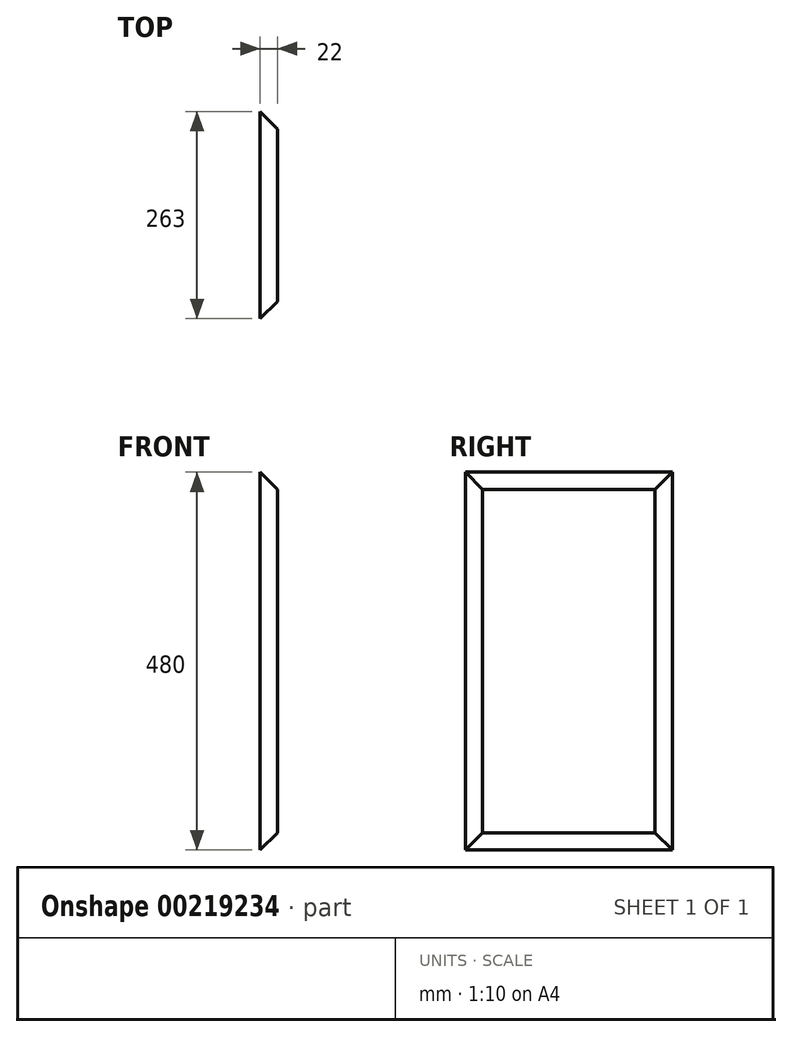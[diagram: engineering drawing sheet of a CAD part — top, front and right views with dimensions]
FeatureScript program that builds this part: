
annotation { "Feature Type Name" : "Feature", "Feature Type Description" : "" }
export const myFeature = defineFeature(function(context is Context, id is Id, definition is map)
    precondition{}
    {
        {
            var Q0;
            Q0=qCreatedBy(makeId("Right.planeOp"),FACE);
            var sketch = newSketch(context, id + "F0", { "sketchPlane" : qUnion([Q0])});
            skLineSegment(sketch, "E0.bottom", {"start": v(-131.5, 240) * mm, "end": v(131.5, 240) * mm});
            skLineSegment(sketch, "E0.top", {"start": v(-131.5, -240) * mm, "end": v(131.5, -240) * mm});
            skLineSegment(sketch, "E0.left", {"start": v(-131.5, 240) * mm, "end": v(-131.5, -240) * mm});
            skLineSegment(sketch, "E0.right", {"start": v(131.5, 240) * mm, "end": v(131.5, -240) * mm});
            skPoint(sketch, "E0.middle", {"position": v(0, 0) * mm});
            skSolve(sketch);
        }
        {
            var Q0;
            Q0=makeQuery(id+"F0.imprint","IMPRINT",FACE,{"disambiguationData":[TD([[makeQuery(id+"F0.imprint","IMPRINT",EDGE,{"derivedFrom":sQuery(id+"F0.wireOp",EDGE,"E0.bottom")}),-1.0]])]});
            extrude(context, id + "F1", {"entities" : qUnion([Q0]), "depth" : 22 * mm});
        }
        {
            var Q0;
            Q0=makeQuery(id+"F1.opExtrude","CAP_EDGE",EDGE,{"disambiguationData":[OSD([sQuery(id+"F0.wireOp",EDGE,"E0.left")])],"isStart":false});
            var Q1;
            Q1=makeQuery(id+"F1.opExtrude","CAP_EDGE",EDGE,{"disambiguationData":[OSD([sQuery(id+"F0.wireOp",EDGE,"E0.top")])],"isStart":false});
            var Q2;
            Q2=makeQuery(id+"F1.opExtrude","CAP_EDGE",EDGE,{"disambiguationData":[OSD([sQuery(id+"F0.wireOp",EDGE,"E0.right")])],"isStart":false});
            var Q3;
            Q3=makeQuery(id+"F1.opExtrude","CAP_EDGE",EDGE,{"disambiguationData":[OSD([sQuery(id+"F0.wireOp",EDGE,"E0.bottom")])],"isStart":false});
            chamfer(context, id + "F2", {"entities" : qUnion([Q0, Q1, Q2, Q3]), "width" : 22 * mm, "tangentPropagation" : true});
        }
    });
